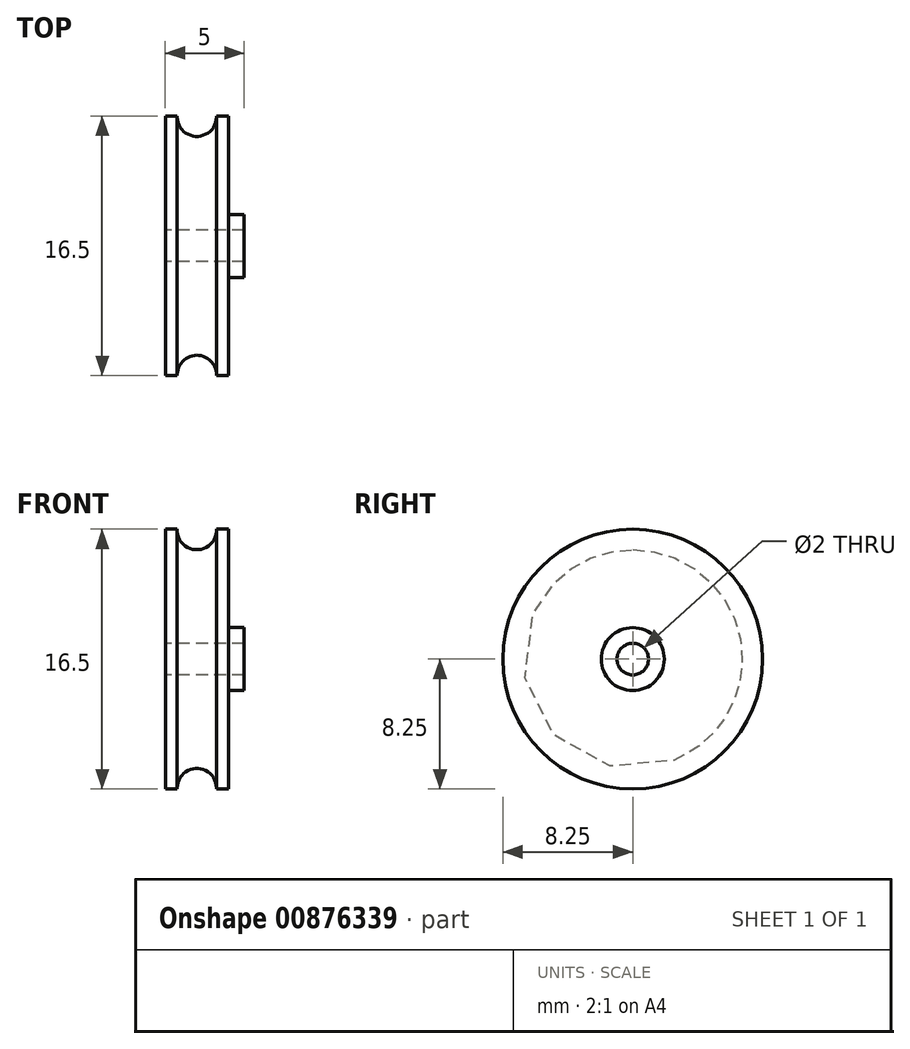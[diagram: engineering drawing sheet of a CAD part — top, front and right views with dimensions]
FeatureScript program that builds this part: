
annotation { "Feature Type Name" : "Feature", "Feature Type Description" : "" }
export const myFeature = defineFeature(function(context is Context, id is Id, definition is map)
    precondition{}
    {
        {
            var Q0;
            Q0=qCreatedBy(makeId("Top.planeOp"),FACE);
            var sketch = newSketch(context, id + "F0", { "sketchPlane" : qUnion([Q0])});
            skLineSegment(sketch, "E0", {"start": v(-3.07, 0) * mm, "end": v(-3.07, 8.25) * mm});
            skLineSegment(sketch, "E1", {"start": v(-3.07, 8.25) * mm, "end": v(-2.32, 8.25) * mm});
            skLineSegment(sketch, "E2", {"start": v(0.93, 0) * mm, "end": v(0.93, 8.25) * mm});
            skLineSegment(sketch, "E3.bottom", {"start": v(0.93, 0) * mm, "end": v(1.93, 0) * mm});
            skLineSegment(sketch, "E3.top", {"start": v(0.93, 2) * mm, "end": v(1.93, 2) * mm});
            skLineSegment(sketch, "E3.left", {"start": v(0.93, 0) * mm, "end": v(0.93, 2) * mm});
            skLineSegment(sketch, "E3.right", {"start": v(1.93, 0) * mm, "end": v(1.93, 2) * mm});
            skLineSegment(sketch, "E4", {"start": v(-3.07, 1) * mm, "end": v(1.93, 1) * mm});
            skLineSegment(sketch, "E5", {"start": v(0.93, 8.25) * mm, "end": v(0.18, 8.25) * mm});
            skArc(sketch, "E6", {"start": v(-2.32, 8.25) * mm, "mid": v(-1.07, 6.95) * mm, "end": v(0.18, 8.25) * mm});
            skLineSegment(sketch, "E7", {"start": v(-5.51, 0) * mm, "end": v(5.72, 0) * mm});
            skSolve(sketch);
        }
        {
            var Q0;
            {var subQ1=sQuery(id+"F0.wireOp",EDGE,"E1");Q0=makeQuery(id+"F0.imprint","IMPRINT",FACE,{"disambiguationData":[TD([[makeQuery(id+"F0.imprint","IMPRINT",EDGE,{"derivedFrom":subQ1}),-1.0]])]});}
            var Q1;
            {var subQ0=sQuery(id+"F0.wireOp",EDGE,"E3.top");Q1=makeQuery(id+"F0.imprint","IMPRINT",FACE,{"disambiguationData":[TD([[makeQuery(id+"F0.imprint","IMPRINT",EDGE,{"derivedFrom":subQ0}),-1.0]])]});}
            var Q2;
            Q2=sQuery(id+"F0.wireOp",EDGE,"E7");
            revolve(context, id + "F1", {"surfaceOperationType" : NewSurfaceOperationType.NEW, "entities" : qUnion([Q0, Q1]), "axis" : qUnion([Q2]), "revolveType" : RevolveType.FULL});
        }
    });
